# Revit family: MI-VB-SM
name_source: partatom
category: Generic Models
revit_build: Autodesk Revit 2018 (Build: 20170223_1515(x64)
units: mm (PartAtom-declared; Revit-internal decimal feet)

## family parameters
Can host rebar = No
Cut with Voids When Loaded = No
Host = Face
Part Type = Normal
Room Calculation Point = No
Round Connector Dimension = Use Diameter
Shared = No

## types (12) — shared parameters
Default Elevation = 4' - 0"
Description = VALVE BOX
Manufacturer = MIFAB
Material = <By Category>
Model = MI-VB-SM
URL = WWW.MIFAB.COM

## per-type parameters (varying)
| type | Depth | Height | Width |
| 8” x 8” x 4” | 0' - 4" | 0' - 8" | 0' - 8" |
| 8” x 8” x 6” | 0' - 6" | 0' - 8" | 0' - 8" |
| 8” x 8” x 8” | 0' - 8" | 0' - 8" | 0' - 8" |
| 12” x 12” x 4” | 0' - 4" | 1' - 0" | 1' - 0" |
| 12” x 12” x 6” | 0' - 6" | 1' - 0" | 1' - 0" |
| 12” x 12” x 8” | 0' - 8" | 1' - 0" | 1' - 0" |
| 14” x 14” x 4” | 0' - 4" | 1' - 2" | 1' - 2" |
| 14” x 14” x 6” | 0' - 6" | 1' - 2" | 1' - 2" |
| 14” x 14” x 8” | 0' - 8" | 1' - 2" | 1' - 2" |
| 16” x 16” x 4” | 0' - 4" | 1' - 4" | 1' - 4" |
| 16” x 16” x 6” | 0' - 6" | 1' - 4" | 1' - 4" |
| 16” x 16” x 8” | 0' - 8" | 1' - 4" | 1' - 4" |

## geometry (parser evidence)
native form markers: Sweep x6
no freeform markers — native parametric forms only
